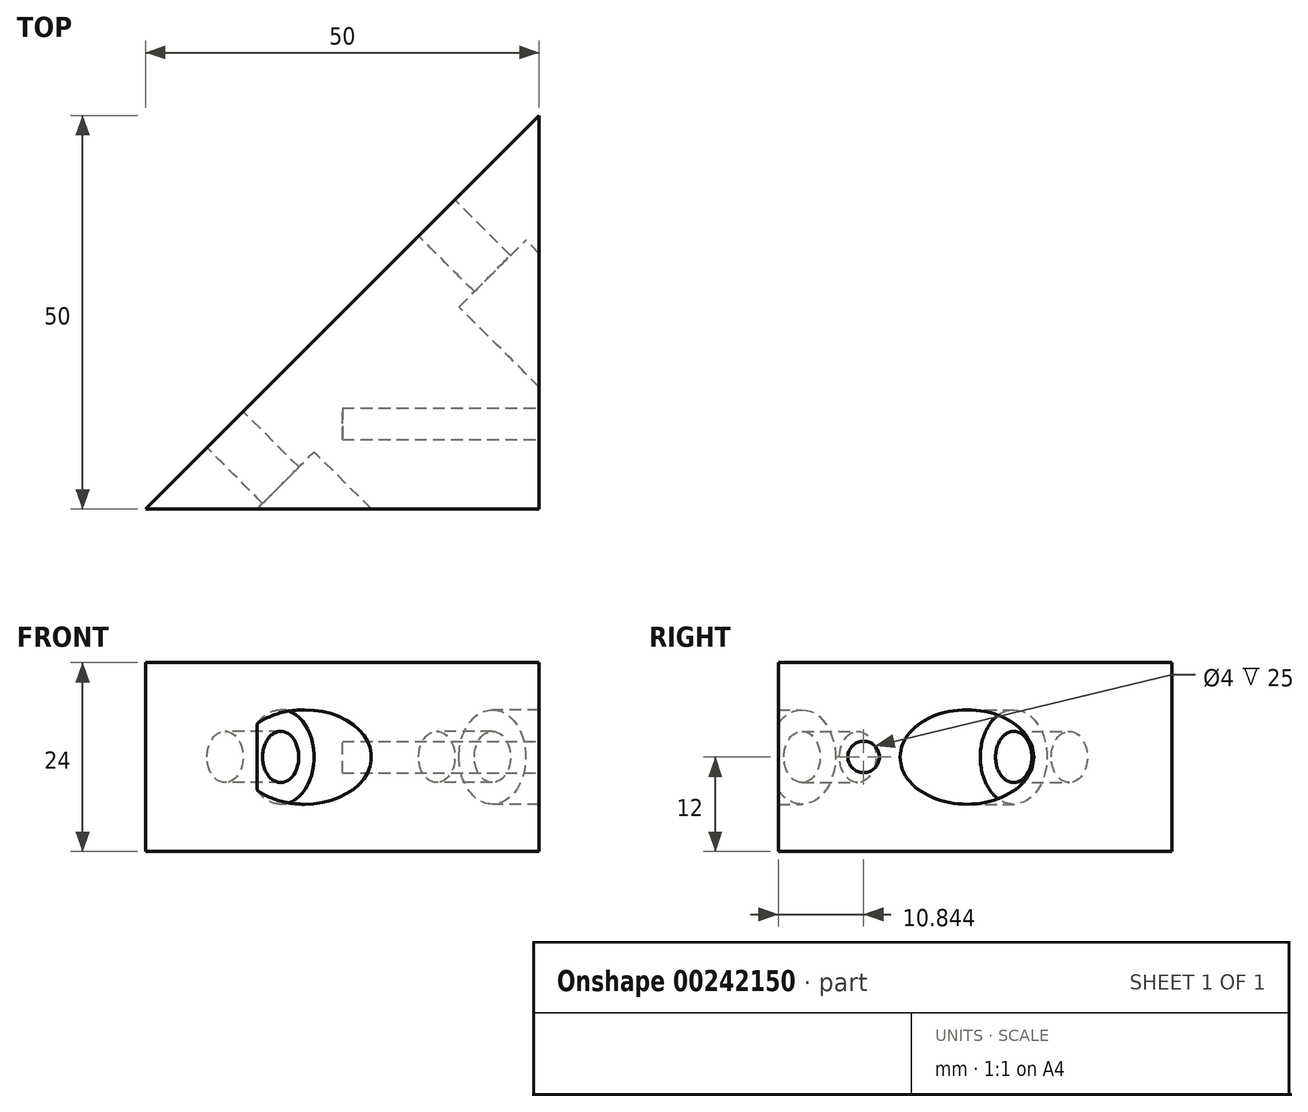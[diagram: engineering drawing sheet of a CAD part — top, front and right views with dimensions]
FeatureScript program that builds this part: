
annotation { "Feature Type Name" : "Feature", "Feature Type Description" : "" }
export const myFeature = defineFeature(function(context is Context, id is Id, definition is map)
    precondition{}
    {
        {
            var Q0;
            Q0=qCreatedBy(makeId("Top.planeOp"),FACE);
            var sketch = newSketch(context, id + "F0", { "sketchPlane" : qUnion([Q0])});
            skLineSegment(sketch, "E0", {"start": v(0, 0) * mm, "end": v(0, 50) * mm});
            skLineSegment(sketch, "E1", {"start": v(0, 50) * mm, "end": v(-50, 0) * mm});
            skLineSegment(sketch, "E2", {"start": v(-50, 0) * mm, "end": v(0, 0) * mm});
            skSolve(sketch);
        }
        {
            var Q0;
            Q0=makeQuery(id+"F0.imprint","IMPRINT",FACE,{"disambiguationData":[TD([[makeQuery(id+"F0.imprint","IMPRINT",EDGE,{"derivedFrom":sQuery(id+"F0.wireOp",EDGE,"E0")}),1.0]])]});
            extrude(context, id + "F1", {"entities" : qUnion([Q0]), "depth" : 24 * mm});
        }
        {
            var Q0;
            Q0=makeQuery(id+"F1.opExtrude","SWEPT_FACE",FACE,{"disambiguationData":[OSD([sQuery(id+"F0.wireOp",EDGE,"E1")])]});
            var sketch = newSketch(context, id + "F2", { "sketchPlane" : qUnion([Q0])});
            skCircle(sketch, "E3", {"center": v(-16.95, 12) * mm, "radius": 3.25 * mm});
            skPoint(sketch, "E3.centerSnap0", {"position": v(-35.36, 12) * mm});
            skCircle(sketch, "E4", {"center": v(21.08, 12) * mm, "radius": 3.25 * mm});
            skPoint(sketch, "E4.centerSnap0", {"position": v(35.36, 12) * mm});
            skCircle(sketch, "E5", {"center": v(-16.95, 12) * mm, "radius": 6 * mm});
            skCircle(sketch, "E6", {"center": v(21.08, 12) * mm, "radius": 6 * mm});
            skSolve(sketch);
        }
        {
            var Q0;
            Q0=makeQuery(id+"F2.imprint","IMPRINT",FACE,{"disambiguationData":[TD([[makeQuery(id+"F2.imprint","IMPRINT",EDGE,{"derivedFrom":sQuery(id+"F2.wireOp",EDGE,"E3")}),1.0]])]});
            var Q1;
            Q1=makeQuery(id+"F2.imprint","IMPRINT",FACE,{"disambiguationData":[TD([[makeQuery(id+"F2.imprint","IMPRINT",EDGE,{"derivedFrom":sQuery(id+"F2.wireOp",EDGE,"E4")}),1.0]])]});
            extrude(context, id + "F3", {"entities" : qUnion([Q0, Q1]), "operationType" : NewBodyOperationType.REMOVE, "oppositeDirection" : true, "depth" : 25 * mm});
        }
        {
            var Q0;
            Q0=makeQuery(id+"F2.imprint","IMPRINT",FACE,{"disambiguationData":[TD([[makeQuery(id+"F2.imprint","IMPRINT",EDGE,{"derivedFrom":sQuery(id+"F2.wireOp",EDGE,"E4")}),-1.0]])]});
            var Q1;
            Q1=makeQuery(id+"F2.imprint","IMPRINT",FACE,{"disambiguationData":[TD([[makeQuery(id+"F2.imprint","IMPRINT",EDGE,{"derivedFrom":sQuery(id+"F2.wireOp",EDGE,"E3")}),-1.0]])]});
            extrude(context, id + "F4", {"entities" : qUnion([Q0, Q1]), "operationType" : NewBodyOperationType.REMOVE, "oppositeDirection" : true, "depth" : 25 * mm, "hasSecondDirection" : true, "secondDirectionOppositeDirection" : true, "secondDirectionDepth" : 10 * mm});
        }
        {
            var Q0;
            Q0=makeQuery(id+"F1.opExtrude","SWEPT_FACE",FACE,{"disambiguationData":[OSD([sQuery(id+"F0.wireOp",EDGE,"E0")])]});
            var sketch = newSketch(context, id + "F5", { "sketchPlane" : qUnion([Q0])});
            skPoint(sketch, "E7", {"position": v(10.84, 12) * mm});
            skPoint(sketch, "E7.positionSnap0", {"position": v(0, 12) * mm});
            skCircle(sketch, "E8", {"center": v(10.84, 12) * mm, "radius": 2 * mm});
            skSolve(sketch);
        }
        {
            var Q0;
            Q0=makeQuery(id+"F5.imprint","IMPRINT",FACE,{"disambiguationData":[TD([[makeQuery(id+"F5.imprint","IMPRINT",EDGE,{"derivedFrom":sQuery(id+"F5.wireOp",EDGE,"E8")}),1.0]])]});
            extrude(context, id + "F6", {"entities" : qUnion([Q0]), "operationType" : NewBodyOperationType.REMOVE, "oppositeDirection" : true, "depth" : 25 * mm});
        }
    });
